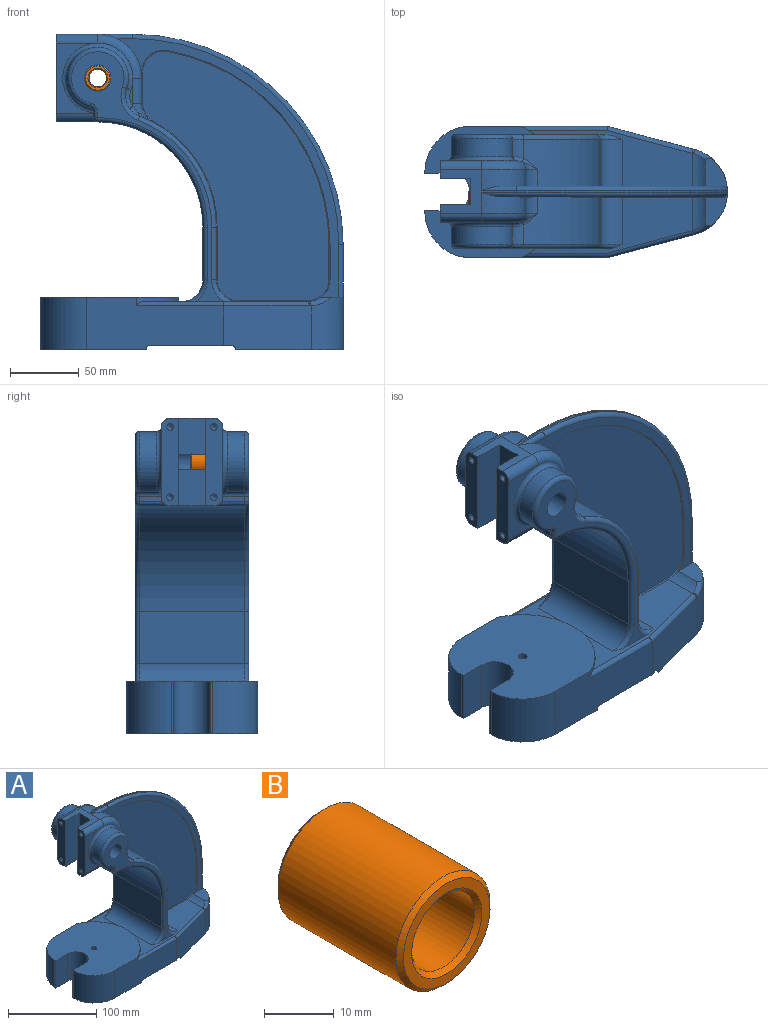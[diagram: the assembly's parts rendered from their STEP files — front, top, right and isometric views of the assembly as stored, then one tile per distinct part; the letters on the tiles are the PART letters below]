
ASSEMBLY  parts=2 mates=1
PART A: 180 faces, bbox 234.5x98.1x244 mm
  f0: plane 63.5x12.7mm, normal (-1,0,0), area 753.5mm2, adj f2,f15,f17,f92,f97,f149,f151,f158
  f1: plane 20.23x2.34mm, normal (0,1,0), area 23.9mm2, adj f90,f91,f104,f106
  f2: plane 50.8x30.1mm, normal (0,-1,0), area 515.4mm2, adj f0,f83,f92,f97,f124
  f3: plane 22.59x12.73mm, normal (1,0,0), area 235.4mm2, adj f19,f26,f32,f87,f94,f174
  f4: plane 22.59x12.73mm, normal (1,0,0), area 235.4mm2, adj f10,f14,f33,f86,f90,f164
  f5: plane 99.19x38.1mm, normal (0,-1,0), area 3202mm2, adj f6,f40,f46,f49,f52,f58,f76,f133
  f6: plane 100x95.25mm, normal (0,0,1), area 7398mm2, adj f5,f43,f44,f48,f54,f55,f56,f57
  f7: plane 38.1x34.96mm, normal (1,0,0), area 1331.9mm2, adj f8,f9,f114,f169
  f8: cylinder r=15.88mm len=34.96mm, axis (0,1,0), area 871.7mm2, adj f7,f37,f115,f167
  f9: cylinder r=85.72mm len=80.21mm, axis (0,1,0), area 3442.3mm2, adj f7,f80,f86,f100,f113,f168
  f10: cylinder r=15.88mm len=18.65mm, axis (0,1,0), area 22.7mm2, adj f4,f11,f33,f162
  f11: cylinder r=142.88mm len=140.67mm, axis (0,1,0), area 163.3mm2, adj f10,f12,f33,f160
  f12: plane 25.4x0.82mm, normal (-1,0,0), area 20.8mm2, adj f11,f13,f33,f161
  f13: cylinder r=15.88mm len=24.81mm, axis (0,1,0), area 242.1mm2, adj f12,f33,f37,f45,f139,f140,f163
  f14: cylinder r=31.75mm len=31.75mm, axis (0,1,0), area 616.8mm2, adj f4,f15,f33,f89,f141
  f15: plane 55.5x31.75mm, normal (0,0,1), area 573.2mm2, adj f0,f14,f16,f19,f31,f88,f92,f141
  f16: plane 63.5x12.7mm, normal (-1,0,0), area 753.5mm2, adj f15,f17,f21,f88,f96,f147,f153,f157
  f17: plane 31.75x30.1mm, normal (0,0,-1), area 533.2mm2, adj f0,f16,f18,f96,f97,f156,f157,f158
  f18: cylinder r=76.2mm len=76.2mm, axis (0,1,0), area 9120.7mm2, adj f17,f22,f103,f105,f119,f121
  f19: cylinder r=31.75mm len=31.75mm, axis (0,1,0), area 616.8mm2, adj f3,f15,f32,f93,f144
  f20: plane 20.23x2.34mm, normal (0,-1,0), area 23.9mm2, adj f94,f95,f122,f124
  f21: plane 50.8x30.1mm, normal (0,1,0), area 515.4mm2, adj f16,f78,f88,f96,f106
  f22: plane 76.2x38.1mm, normal (-1,0,0), area 2903.2mm2, adj f18,f98,f101,f117
  f23: cylinder r=15.88mm len=34.96mm, axis (0,1,0), area 871.7mm2, adj f24,f37,f132,f177
  f24: plane 38.1x34.96mm, normal (1,0,0), area 1331.9mm2, adj f23,f25,f131,f179
  f25: cylinder r=85.72mm len=80.21mm, axis (0,1,0), area 3442.3mm2, adj f24,f81,f87,f118,f130,f178
  f26: cylinder r=15.88mm len=18.65mm, axis (0,1,0), area 22.7mm2, adj f3,f27,f32,f172
  f27: cylinder r=142.88mm len=140.67mm, axis (0,1,0), area 163.3mm2, adj f26,f28,f32,f170
  f28: plane 25.4x0.82mm, normal (-1,0,0), area 20.8mm2, adj f27,f29,f32,f171
  f29: cylinder r=15.88mm len=24.81mm, axis (0,1,0), area 242.1mm2, adj f28,f32,f36,f37,f135,f136,f173
  f30: plane 76.2x7.92mm, normal (1,0,0), area 361.9mm2, adj f31,f36,f42,f45,f51,f53,f143,f146
  f31: cylinder r=152.4mm len=152.4mm, axis (0,1,0), area 377mm2, adj f15,f30,f142,f145
  f32: plane 187.33x160.79mm, normal (0,-1,0), area 1900.4mm2, adj f3,f19,f26,f27,f28,f29,f36,f144
  f33: plane 187.33x160.79mm, normal (0,1,0), area 1900.4mm2, adj f4,f10,f11,f12,f13,f14,f45,f141
  f34: plane 180.67x135mm, normal (0,-1,0), area 14138.8mm2, adj f170,f171,f172,f173,f174,f175,f176,f177
  f35: plane 180.67x135mm, normal (0,1,0), area 14138.8mm2, adj f160,f161,f162,f163,f164,f165,f166,f167
  f36: plane 26.58x18.73mm, normal (0,0,1), area 245.8mm2, adj f29,f30,f32,f53,f136,f146
  f37: plane 119.12x89.67mm, normal (0,0,1), area 4280.2mm2, adj f8,f13,f23,f29,f76,f77,f84,f98
  f38: cylinder r=3.17mm len=9.06mm, axis (0,1,0), area 40.9mm2, adj f40,f42,f52,f69
  f39: cylinder r=3.17mm len=7.93mm, axis (0,1,0), area 39.5mm2, adj f41,f46,f48,f65
  f40: plane 58.73x9.7mm, normal (0,0,-1), area 467.1mm2, adj f5,f38,f49,f52,f64,f69
  f41: plane 58.73x9.7mm, normal (0,0,-1), area 467.1mm2, adj f39,f47,f48,f50,f65,f67
  f42: plane 90.55x77.8mm, normal (0,0,-1), area 1454mm2, adj f30,f38,f47,f50,f51,f52,f53,f59
  f43: plane 38.1x1.61mm, normal (-1,0,0), area 61.5mm2, adj f6,f46,f54,f58
  f44: plane 38.1x1.61mm, normal (-1,0,0), area 61.5mm2, adj f6,f46,f55,f57
  f45: plane 26.58x18.73mm, normal (0,0,1), area 245.8mm2, adj f13,f30,f33,f51,f140,f143
  f46: plane 95.25x76.2mm, normal (0,0,-1), area 2029.8mm2, adj f5,f39,f43,f44,f48,f49,f54,f55
  f47: cylinder r=3.17mm len=9.06mm, axis (0,1,0), area 40.9mm2, adj f41,f42,f50,f67
  f48: plane 99.19x38.1mm, normal (0,1,0), area 3202mm2, adj f6,f39,f41,f46,f50,f57,f76,f137
  f49: cylinder r=3.17mm len=7.93mm, axis (0,1,0), area 39.5mm2, adj f5,f40,f46,f64
  f50: plane 63.64x32.15mm, normal (0.26,0.97,0), area 2053.6mm2, adj f41,f42,f47,f48,f51,f138,f139
  f51: cylinder r=31.75mm len=38.1mm, axis (0,0,-1), area 1379.2mm2, adj f30,f42,f45,f50,f140
  f52: plane 63.64x32.15mm, normal (0.26,-0.97,0), area 2053.6mm2, adj f5,f38,f40,f42,f53,f134,f135
  f53: cylinder r=31.75mm len=38.1mm, axis (0,0,-1), area 1379.2mm2, adj f30,f36,f42,f52,f136
  f54: plane 38.1x19.05mm, normal (0,1,0), area 725.8mm2, adj f6,f43,f46,f56
  f55: plane 38.1x19.05mm, normal (0,-1,0), area 725.8mm2, adj f6,f44,f46,f56
  f56: cylinder r=13.49mm len=38.1mm, axis (0,0,-1), area 1615.1mm2, adj f6,f46,f54,f55
  f57: cylinder r=33.32mm len=38.1mm, axis (0,0,-1), area 1963.7mm2, adj f6,f44,f46,f48
  f58: cylinder r=33.32mm len=38.1mm, axis (0,0,-1), area 1963.7mm2, adj f5,f6,f43,f46
  f59: plane 30.18x6.86mm, normal (-1,0,0), area 207mm2, adj f42,f60,f68,f70
  f60: plane 31.27x5.6mm, normal (0,0,-1), area 124.1mm2, adj f59,f61,f68,f70
  f61: cylinder r=23.8mm len=46.06mm, axis (0,1,0), area 499.2mm2, adj f60,f62,f67,f68,f69,f70
  f62: plane 84.13x79.4mm, normal (0,0,-1), area 5642.5mm2, adj f61,f64,f65,f66,f67,f69
  f63: plane 100.62x79.4mm, normal (0,0,-1), area 6568.5mm2, adj f64,f65,f66,f71,f72,f73,f74,f75
  f64: plane 98.15x30.18mm, normal (0,1,0), area 2718.8mm2, adj f40,f46,f49,f62,f63,f66,f69,f75
  f65: plane 98.15x30.18mm, normal (0,-1,0), area 2718.8mm2, adj f39,f41,f46,f62,f63,f66,f67,f74
  f66: plane 79.4x3.18mm, normal (-1,0,0), area 252.1mm2, adj f62,f63,f64,f65
  f67: plane 62.63x27.36mm, normal (-0.26,-0.97,0), area 1710.8mm2, adj f41,f42,f47,f61,f62,f65,f68
  f68: cylinder r=23.83mm len=30.18mm, axis (0,0,-1), area 814.8mm2, adj f42,f59,f60,f61,f67
  f69: plane 62.63x27.36mm, normal (-0.26,0.97,0), area 1710.8mm2, adj f38,f40,f42,f61,f62,f64,f70
  f70: cylinder r=23.83mm len=30.18mm, axis (0,0,-1), area 814.8mm2, adj f42,f59,f60,f61,f69
  f71: plane 30.18x10.12mm, normal (0,-1,0), area 305.3mm2, adj f46,f63,f73,f75
  f72: plane 30.18x10.12mm, normal (0,1,0), area 305.3mm2, adj f46,f63,f73,f74
  f73: cylinder r=21.42mm len=42.84mm, axis (0,0,-1), area 2030.4mm2, adj f46,f63,f71,f72
  f74: cylinder r=25.4mm len=30.18mm, axis (0,0,-1), area 986.2mm2, adj f46,f63,f65,f72
  f75: cylinder r=25.4mm len=30.18mm, axis (0,0,-1), area 986.2mm2, adj f46,f63,f64,f71
  f76: cylinder r=52.37mm len=95.25mm, axis (0,0,1), area 401mm2, adj f5,f6,f37,f48,f133,f137
  f77: plane 180.98x110.12mm, normal (0,1,0), area 1717.8mm2, adj f37,f85,f99,f101,f103,f109,f110,f111
  f78: plane 16.73x3.98mm, normal (-1,0,0), area 64.1mm2, adj f21,f96,f105,f106,f108,f109
  f79: cylinder r=22.23mm len=44.45mm, axis (0,1,0), area 1356.2mm2, adj f80,f106,f108,f111
  f80: cylinder r=15.88mm len=20.22mm, axis (0,1,0), area 319.4mm2, adj f9,f79,f102,f104,f112
  f81: cylinder r=15.88mm len=20.22mm, axis (0,1,0), area 319.4mm2, adj f25,f82,f120,f122,f129
  f82: cylinder r=22.23mm len=44.45mm, axis (0,1,0), area 1356.2mm2, adj f81,f124,f126,f128
  f83: plane 16.73x3.98mm, normal (-1,0,0), area 64.1mm2, adj f2,f97,f121,f124,f125,f126
  f84: plane 180.98x110.12mm, normal (0,-1,0), area 1717.8mm2, adj f37,f85,f116,f117,f119,f125,f127,f128
  f85: cylinder r=9.53mm len=82.55mm, axis (0,1,0), area 4727mm2, adj f77,f84,f156,f157,f158,f159
  f86: cylinder r=15.88mm len=14.02mm, axis (0,1,0), area 218.9mm2, adj f4,f9,f91,f166
  f87: cylinder r=15.88mm len=14.02mm, axis (0,1,0), area 218.9mm2, adj f3,f25,f95,f176
  f88: cylinder r=6.35mm len=30.1mm, axis (-1,0,0), area 300.2mm2, adj f15,f16,f21,f89
  f89: torus R=25.4mm, axis (0,-1,0), area 461.3mm2, adj f14,f88,f90,f106
  f90: cylinder r=6.35mm len=18.2mm, axis (0,0,1), area 181.6mm2, adj f1,f4,f89,f91
  f91: torus R=22.23mm, axis (0,-1,0), area 98mm2, adj f1,f86,f90,f100,f102
  f92: cylinder r=6.35mm len=30.1mm, axis (1,0,0), area 300.2mm2, adj f0,f2,f15,f93
  f93: torus R=25.4mm, axis (0,-1,0), area 461.3mm2, adj f19,f92,f94,f124
  f94: cylinder r=6.35mm len=18.2mm, axis (0,0,-1), area 181.6mm2, adj f3,f20,f93,f95
  f95: torus R=22.23mm, axis (0,-1,0), area 98mm2, adj f20,f87,f94,f118,f120
  f96: cylinder r=6.35mm len=30.1mm, axis (1,0,0), area 279.1mm2, adj f16,f17,f21,f78,f105
  f97: cylinder r=6.35mm len=30.1mm, axis (-1,0,0), area 279.1mm2, adj f0,f2,f17,f83,f121
  f98: cylinder r=15.88mm len=76.2mm, axis (0,-1,0), area 1900.2mm2, adj f22,f37,f99,f116
  f99: torus R=19.05mm, axis (0,-1,0), area 107.7mm2, adj f37,f77,f98,f101
  f100: bspline ~12.01x8.85mm, area 17.9mm2, adj f9,f91,f102
  f101: cylinder r=3.17mm len=38.1mm, axis (0,0,-1), area 190mm2, adj f22,f77,f99,f103
  f102: bspline ~10.6x9.56mm, area 36.6mm2, adj f80,f91,f100,f104
  f103: torus R=79.38mm, axis (0,-1,0), area 606mm2, adj f18,f77,f101,f107
  f104: torus R=12.7mm, axis (0,-1,0), area 70.6mm2, adj f1,f80,f102,f106
  f105: cylinder r=3.17mm len=22.23mm, axis (0,1,0), area 97.1mm2, adj f18,f78,f96,f107
  f106: torus R=25.4mm, axis (0,-1,0), area 570mm2, adj f1,f21,f78,f79,f89,f104,f108
  f107: sphere r=3.17mm, area 21.6mm2, adj f103,f105,f109
  f108: cylinder r=3.17mm len=15.82mm, axis (0,1,0), area 59.7mm2, adj f78,f79,f106,f110
  f109: cylinder r=3.17mm len=3.98mm, axis (0,0,-1), area 19.9mm2, adj f77,f78,f107,f110
  f110: torus R=6.35mm, axis (0,-1,0), area 28.5mm2, adj f77,f108,f109,f111
  f111: torus R=19.05mm, axis (0,-1,0), area 504.9mm2, adj f77,f79,f110,f112
  f112: torus R=19.05mm, axis (0,-1,0), area 132.1mm2, adj f77,f80,f111,f113
  f113: torus R=82.55mm, axis (0,-1,0), area 510.4mm2, adj f9,f77,f112,f114
  f114: cylinder r=3.17mm len=38.1mm, axis (0,0,1), area 190mm2, adj f7,f77,f113,f115
  f115: torus R=19.05mm, axis (0,-1,0), area 107.7mm2, adj f8,f37,f77,f114
  f116: torus R=19.05mm, axis (0,-1,0), area 107.7mm2, adj f37,f84,f98,f117
  f117: cylinder r=3.17mm len=38.1mm, axis (0,0,1), area 190mm2, adj f22,f84,f116,f119
  f118: bspline ~11.06x8.44mm, area 17.9mm2, adj f25,f95,f120
  f119: torus R=79.38mm, axis (0,-1,0), area 606mm2, adj f18,f84,f117,f123
  f120: bspline ~9.12x8.99mm, area 36.6mm2, adj f81,f95,f118,f122
  f121: cylinder r=3.17mm len=22.23mm, axis (0,1,0), area 97.1mm2, adj f18,f83,f97,f123
  f122: torus R=12.7mm, axis (0,-1,0), area 70.6mm2, adj f20,f81,f120,f124
  f123: sphere r=3.17mm, area 15.8mm2, adj f119,f121,f125
  f124: torus R=25.4mm, axis (0,-1,0), area 570mm2, adj f2,f20,f82,f83,f93,f122,f126
  f125: cylinder r=3.17mm len=3.98mm, axis (0,0,1), area 19.9mm2, adj f83,f84,f123,f127
  f126: cylinder r=3.17mm len=15.82mm, axis (0,1,0), area 59.7mm2, adj f82,f83,f124,f127
  f127: torus R=6.35mm, axis (0,-1,0), area 28.5mm2, adj f84,f125,f126,f128
  f128: torus R=19.05mm, axis (0,-1,0), area 504.9mm2, adj f82,f84,f127,f129
  f129: torus R=19.05mm, axis (0,-1,0), area 132.1mm2, adj f81,f84,f128,f130
  f130: torus R=82.55mm, axis (0,-1,0), area 510.4mm2, adj f25,f84,f129,f131
  f131: cylinder r=3.17mm len=38.1mm, axis (0,0,-1), area 190mm2, adj f24,f84,f130,f132
  f132: torus R=19.05mm, axis (0,-1,0), area 107.7mm2, adj f23,f37,f84,f131
  f133: cylinder r=3.17mm len=63.09mm, axis (1,0,0), area 298.9mm2, adj f5,f37,f76,f134
  f134: cylinder r=3.17mm len=62.81mm, axis (0.97,0.26,0), area 319mm2, adj f37,f52,f133,f135
  f135: bspline ~3.41x3.21mm, area 6mm2, adj f29,f52,f134,f136
  f136: bspline ~18.95x11.92mm, area 79.7mm2, adj f29,f36,f53,f135
  f137: cylinder r=3.17mm len=63.09mm, axis (-1,0,0), area 298.9mm2, adj f37,f48,f76,f138
  f138: cylinder r=3.17mm len=62.81mm, axis (-0.97,0.26,0), area 319mm2, adj f37,f50,f137,f139
  f139: bspline ~6.89x4.84mm, area 6mm2, adj f13,f50,f138,f140
  f140: bspline ~17.46x11.57mm, area 79.7mm2, adj f13,f45,f51,f139
  f141: cylinder r=3.17mm len=25.4mm, axis (-1,0,0), area 92.2mm2, adj f14,f15,f33,f142
  f142: torus R=149.22mm, axis (0,-1,0), area 1184.9mm2, adj f31,f33,f141,f143
  f143: cylinder r=3.17mm len=38.1mm, axis (0,0,1), area 190mm2, adj f30,f33,f45,f142
  f144: cylinder r=3.17mm len=25.4mm, axis (1,0,0), area 92.2mm2, adj f15,f19,f32,f145
  f145: torus R=149.22mm, axis (0,-1,0), area 1184.9mm2, adj f31,f32,f144,f146
  f146: cylinder r=3.17mm len=38.1mm, axis (0,0,-1), area 190mm2, adj f30,f32,f36,f145
  f147: cylinder r=2.38mm len=6.35mm, axis (-1,0,0), area 95mm2, adj f16,f148
  f148: cone r=0mm half-angle=59deg, axis (-1,0,0), area 20.8mm2, adj f147
  f149: cylinder r=2.38mm len=6.35mm, axis (-1,0,0), area 95mm2, adj f0,f150
  f150: cone r=0mm half-angle=59deg, axis (-1,0,0), area 20.8mm2, adj f149
  f151: cylinder r=2.38mm len=6.35mm, axis (-1,0,0), area 95mm2, adj f0,f152
  f152: cone r=0mm half-angle=59deg, axis (-1,0,0), area 20.8mm2, adj f151
  f153: cylinder r=2.38mm len=6.35mm, axis (-1,0,0), area 95mm2, adj f16,f154
  f154: cone r=0mm half-angle=59deg, axis (-1,0,0), area 20.8mm2, adj f153
  f155: cylinder r=3.17mm len=7.93mm, axis (0,0,1), area 158.1mm2, adj f6,f63
  f156: plane 26.47x19.05mm, normal (-1,0,0), area 504.2mm2, adj f17,f85,f157,f158
  f157: plane 63.5x22.17mm, normal (0,-1,0), area 1396.6mm2, adj f15,f16,f17,f85,f156,f159
  f158: plane 63.5x22.17mm, normal (0,1,0), area 1396.6mm2, adj f0,f15,f17,f85,f156,f159
  f159: plane 26.47x19.05mm, normal (-1,0,0), area 504.2mm2, adj f15,f85,f157,f158
  f160: torus R=142.11mm, axis (0,-1,0), area 238.1mm2, adj f11,f35,f161,f162
  f161: cylinder r=0.76mm len=25.4mm, axis (0,0,1), area 30.4mm2, adj f12,f35,f160,f163
  f162: torus R=15.11mm, axis (0,-1,0), area 32.6mm2, adj f10,f35,f160,f164
  f163: torus R=15.11mm, axis (0,-1,0), area 29.3mm2, adj f13,f35,f161,f165
  f164: cylinder r=0.76mm len=22.59mm, axis (0,0,1), area 27mm2, adj f4,f35,f162,f166
  f165: cylinder r=0.76mm len=50.8mm, axis (1,0,0), area 60.8mm2, adj f35,f37,f163,f167
  f166: torus R=15.11mm, axis (0,-1,0), area 20.2mm2, adj f35,f86,f164,f168
  f167: torus R=15.11mm, axis (0,-1,0), area 29.3mm2, adj f8,f35,f165,f169
  f168: torus R=86.49mm, axis (0,-1,0), area 111.5mm2, adj f9,f35,f166,f169
  f169: cylinder r=0.76mm len=38.1mm, axis (0,0,-1), area 45.6mm2, adj f7,f35,f167,f168
  f170: torus R=142.11mm, axis (0,-1,0), area 238.1mm2, adj f27,f34,f171,f172
  f171: cylinder r=0.76mm len=25.4mm, axis (0,0,-1), area 30.4mm2, adj f28,f34,f170,f173
  f172: torus R=15.11mm, axis (0,-1,0), area 32.6mm2, adj f26,f34,f170,f174
  f173: torus R=15.11mm, axis (0,-1,0), area 29.3mm2, adj f29,f34,f171,f175
  f174: cylinder r=0.76mm len=22.59mm, axis (0,0,-1), area 27mm2, adj f3,f34,f172,f176
  f175: cylinder r=0.76mm len=50.8mm, axis (-1,0,0), area 60.8mm2, adj f34,f37,f173,f177
  f176: torus R=15.11mm, axis (0,-1,0), area 20.2mm2, adj f34,f87,f174,f178
  f177: torus R=15.11mm, axis (0,-1,0), area 29.3mm2, adj f23,f34,f175,f179
  f178: torus R=86.49mm, axis (0,-1,0), area 111.5mm2, adj f25,f34,f176,f179
  f179: cylinder r=0.76mm len=38.1mm, axis (0,0,1), area 45.6mm2, adj f24,f34,f177,f178
PART B: 8 faces, bbox 19.1x25.4x19.1 mm
  f0: plane 17.53x17.53mm, normal (0,-1,0), area 82.3mm2, adj f4,f5
  f1: plane 17.53x17.53mm, normal (0,1,0), area 82.3mm2, adj f6,f7
  f2: cylinder r=9.53mm len=23.88mm, axis (0,1,0), area 1428.9mm2, adj f4,f7
  f3: cylinder r=6.35mm len=23.88mm, axis (0,1,0), area 952.6mm2, adj f5,f6
  f4: cone r=9.53mm half-angle=45deg, axis (0,1,0), area 61.9mm2, adj f0,f2
  f5: cone r=6.35mm half-angle=45deg, axis (0,-1,0), area 45.6mm2, adj f0,f3
  f6: cone r=6.35mm half-angle=45deg, axis (0,1,0), area 45.6mm2, adj f1,f3
  f7: cone r=9.53mm half-angle=45deg, axis (0,-1,0), area 61.9mm2, adj f1,f2
PLACE A t=(-106.79,-67.56,14.57)mm
PLACE B t=(-106.79,-108.08,14.57)mm
MATE cylindrical B.f2 <-> A.f14  axis (0,1,0) through (-106.79,-67.56,14.57)mm
